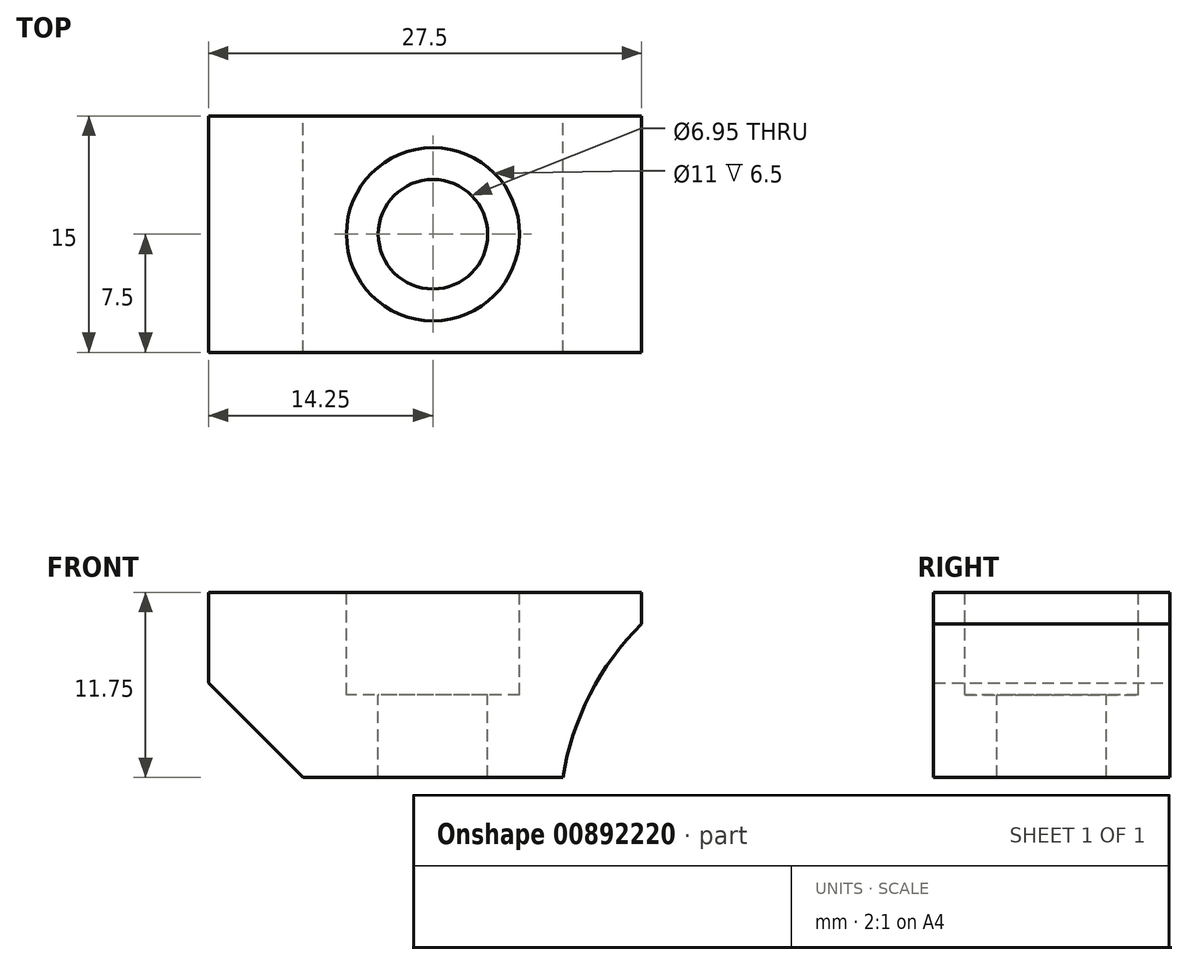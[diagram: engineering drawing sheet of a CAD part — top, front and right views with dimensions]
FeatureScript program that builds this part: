
annotation { "Feature Type Name" : "Feature", "Feature Type Description" : "" }
export const myFeature = defineFeature(function(context is Context, id is Id, definition is map)
    precondition{}
    {
        {
            var Q0;
            Q0=qCreatedBy(makeId("Front.planeOp"),FACE);
            var sketch = newSketch(context, id + "F0", { "sketchPlane" : qUnion([Q0])});
            skLineSegment(sketch, "E0", {"start": v(-13.75, 5.54) * mm, "end": v(-13.75, -0.21) * mm});
            skLineSegment(sketch, "E1", {"start": v(-13.75, -0.21) * mm, "end": v(-7.75, -6.21) * mm});
            skLineSegment(sketch, "E2", {"start": v(-7.75, -6.21) * mm, "end": v(8.76, -6.21) * mm});
            skLineSegment(sketch, "E3", {"start": v(-13.75, 5.54) * mm, "end": v(13.75, 5.54) * mm});
            skLineSegment(sketch, "E4", {"start": v(13.75, 5.54) * mm, "end": v(13.75, 3.54) * mm});
            skArc(sketch, "E5", {"start": v(13.75, 3.54) * mm, "mid": v(10.47, -0.94) * mm, "end": v(8.76, -6.21) * mm});
            skSolve(sketch);
        }
        {
            var Q0;
            Q0=makeQuery(id+"F0.imprint","IMPRINT",FACE,{"disambiguationData":[TD([[makeQuery(id+"F0.imprint","IMPRINT",EDGE,{"derivedFrom":sQuery(id+"F0.wireOp",EDGE,"E0")}),1.0]])]});
            extrude(context, id + "F1", {"entities" : qUnion([Q0]), "depth" : 15 * mm, "offsetDistance" : 25.4 * mm});
        }
        {
            var Q0;
            Q0=makeQuery(id+"F1.opExtrude","SWEPT_FACE",FACE,{"disambiguationData":[OSD([sQuery(id+"F0.wireOp",EDGE,"E3")])]});
            var sketch = newSketch(context, id + "F2", { "sketchPlane" : qUnion([Q0])});
            skPoint(sketch, "E6", {"position": v(0.5, -7.5) * mm});
            skSolve(sketch);
        }
        {
            var Q0;
            Q0=sQuery(id+"F2.wireOp",VERTEX,"E6");
            var Q1;
            Q1=makeQuery(id+"F1.opExtrude","SWEPT_BODY",BODY,{"disambiguationData":[OSD([sQuery(id+"F0.wireOp",EDGE,"E0"),sQuery(id+"F0.wireOp",EDGE,"E1"),sQuery(id+"F0.wireOp",EDGE,"E2"),sQuery(id+"F0.wireOp",EDGE,"E3"),sQuery(id+"F0.wireOp",EDGE,"E4"),sQuery(id+"F0.wireOp",EDGE,"E5")])]});
            hole(context, id + "F3", {"style" : HoleStyle.C_BORE, "endStyle" : HoleEndStyle.THROUGH, "holeDiameter" : 6.95 * mm, "cBoreDiameter" : 11 * mm, "cBoreDepth" : 6.5 * mm, "majorDiameter" : 6.35 * mm, "isTappedThrough" : true, "tappedDepth" : 12.7 * mm, "tapClearance" : 3, "locations" : qUnion([Q0]), "scope" : qUnion([Q1])});
        }
    });
